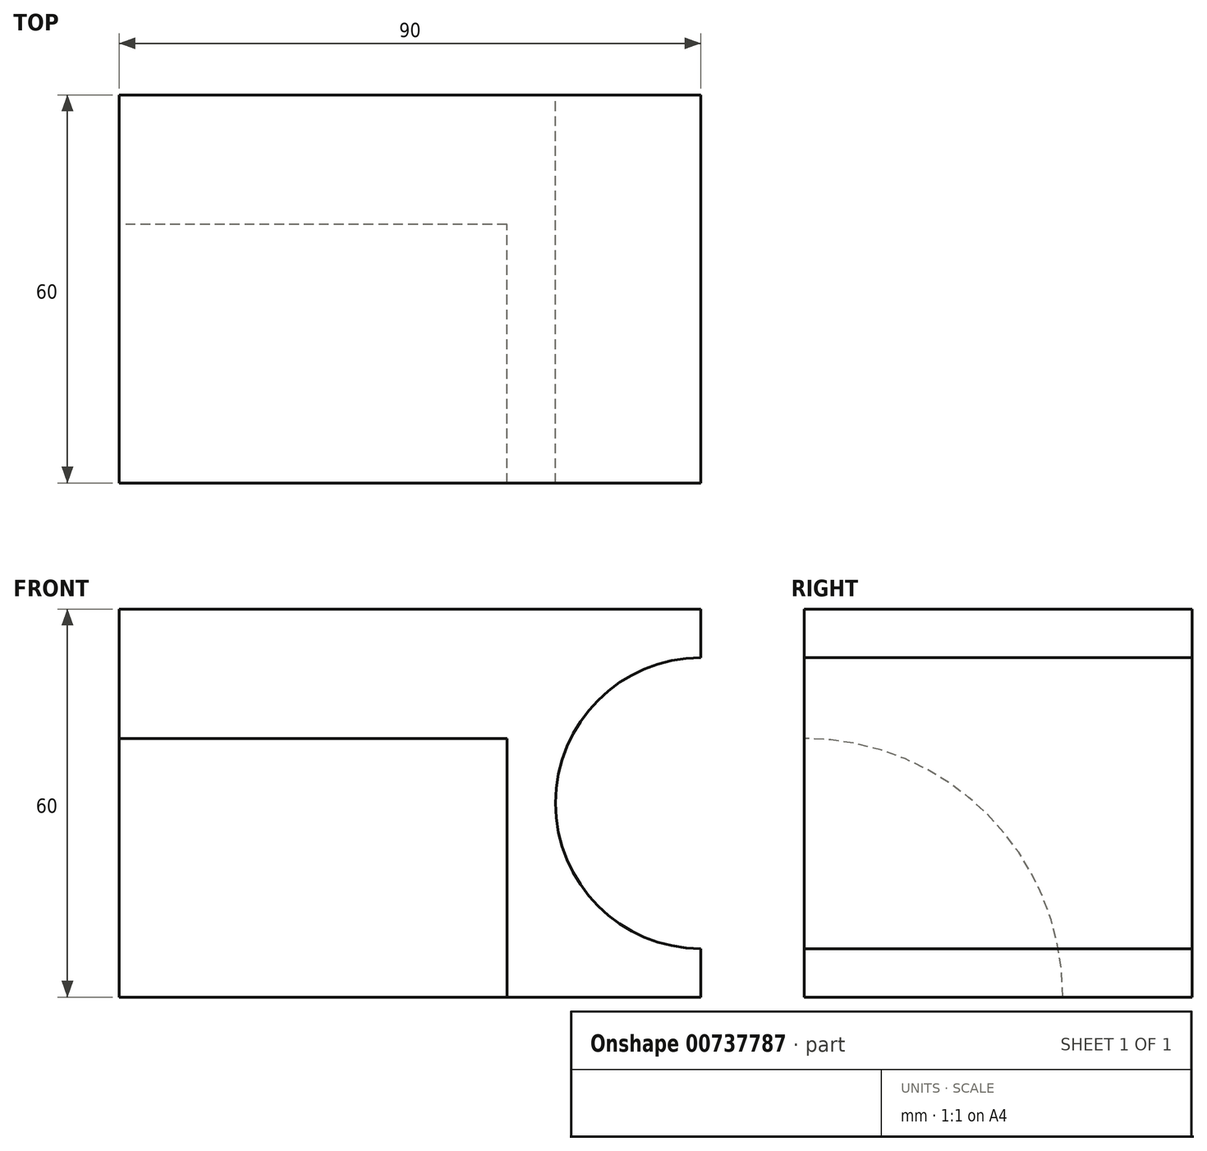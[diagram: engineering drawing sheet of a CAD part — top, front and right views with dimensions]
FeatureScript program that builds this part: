
annotation { "Feature Type Name" : "Feature", "Feature Type Description" : "" }
export const myFeature = defineFeature(function(context is Context, id is Id, definition is map)
    precondition{}
    {
        {
            var Q0;
            Q0=qCreatedBy(makeId("Front.planeOp"),FACE);
            var sketch = newSketch(context, id + "F0", { "sketchPlane" : qUnion([Q0])});
            skLineSegment(sketch, "E0", {"start": v(0, 0) * mm, "end": v(90, 0) * mm});
            skLineSegment(sketch, "E1", {"start": v(90, 60) * mm, "end": v(0, 60) * mm});
            skLineSegment(sketch, "E2", {"start": v(0, 60) * mm, "end": v(0, 0) * mm});
            skArc(sketch, "E3", {"start": v(90, 52.5) * mm, "mid": v(67.5, 30) * mm, "end": v(90, 7.5) * mm});
            skLineSegment(sketch, "E4", {"start": v(90, 60) * mm, "end": v(90, 52.5) * mm});
            skLineSegment(sketch, "E5", {"start": v(90, 7.5) * mm, "end": v(90, 0) * mm});
            skSolve(sketch);
        }
        {
            var Q0;
            Q0 = qSketchRegion(id + "F0", true);
            extrude(context, id + "F1", {"entities" : qUnion([Q0]), "depth" : 60 * mm, "offsetDistance" : 25 * mm});
        }
        {
            var Q0;
            Q0=makeQuery(id+"F1.opExtrude","SWEPT_FACE",FACE,{"disambiguationData":[OSD([sQuery(id+"F0.wireOp",EDGE,"E2")])]});
            var sketch = newSketch(context, id + "F2", { "sketchPlane" : qUnion([Q0])});
            skArc(sketch, "E6", {"start": v(60, 40) * mm, "mid": v(31.72, 28.28) * mm, "end": v(20, 0) * mm});
            skSolve(sketch);
        }
        {
            var Q0;
            {var subQ0=sQuery(id+"F2.wireOp",EDGE,"E6");Q0=makeQuery(id+"F2.imprint","IMPRINT",FACE,{"disambiguationData":[TD([[makeQuery(id+"F2.imprint","IMPRINT",EDGE,{"derivedFrom":subQ0}),1.0]])]});}
            extrude(context, id + "F3", {"entities" : qUnion([Q0]), "operationType" : NewBodyOperationType.REMOVE, "oppositeDirection" : true, "depth" : 60 * mm, "offsetDistance" : 25 * mm});
        }
    });
